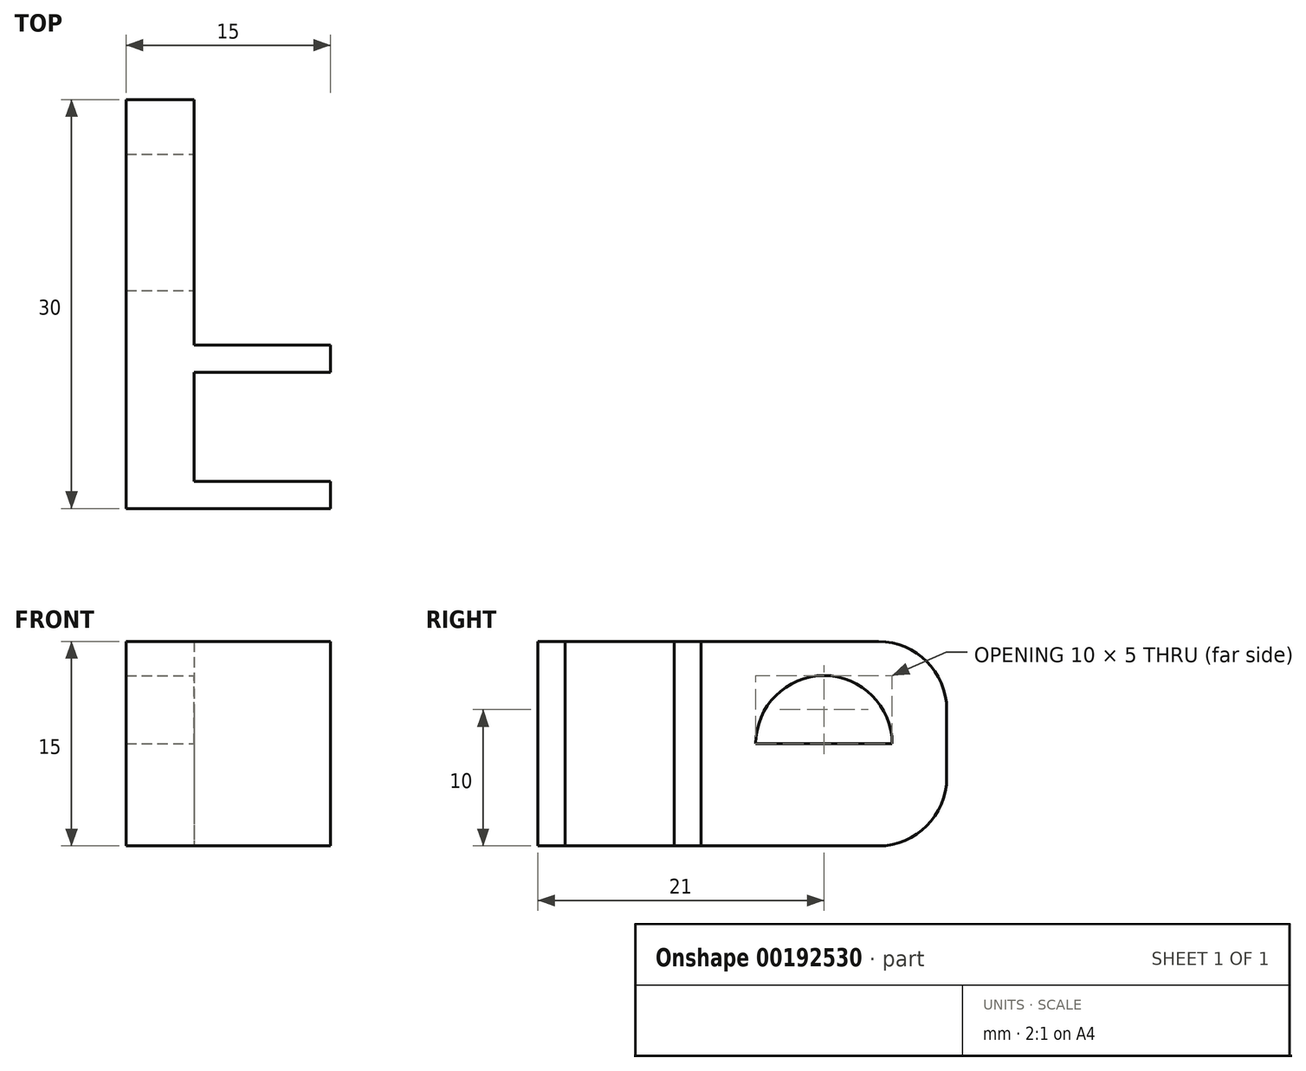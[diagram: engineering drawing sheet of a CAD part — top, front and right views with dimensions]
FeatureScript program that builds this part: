
annotation { "Feature Type Name" : "Feature", "Feature Type Description" : "" }
export const myFeature = defineFeature(function(context is Context, id is Id, definition is map)
    precondition{}
    {
        {
            var Q0;
            Q0=qCreatedBy(makeId("Top.planeOp"),FACE);
            var sketch = newSketch(context, id + "F0", { "sketchPlane" : qUnion([Q0])});
            skLineSegment(sketch, "E0.bottom", {"start": v(0, 0) * mm, "end": v(5, 0) * mm});
            skLineSegment(sketch, "E0.top", {"start": v(0, 30) * mm, "end": v(5, 30) * mm});
            skLineSegment(sketch, "E0.left", {"start": v(0, 0) * mm, "end": v(0, 30) * mm});
            skLineSegment(sketch, "E0.right", {"start": v(5, 0) * mm, "end": v(5, 30) * mm});
            skLineSegment(sketch, "E1.bottom", {"start": v(5, 2) * mm, "end": v(15, 2) * mm});
            skLineSegment(sketch, "E1.top", {"start": v(5, 0) * mm, "end": v(15, 0) * mm});
            skLineSegment(sketch, "E1.left", {"start": v(5, 2) * mm, "end": v(5, 0) * mm});
            skLineSegment(sketch, "E1.right", {"start": v(15, 2) * mm, "end": v(15, 0) * mm});
            skLineSegment(sketch, "E2.bottom", {"start": v(5, 12) * mm, "end": v(15, 12) * mm});
            skLineSegment(sketch, "E2.top", {"start": v(5, 10) * mm, "end": v(15, 10) * mm});
            skLineSegment(sketch, "E2.left", {"start": v(5, 12) * mm, "end": v(5, 10) * mm});
            skLineSegment(sketch, "E2.right", {"start": v(15, 12) * mm, "end": v(15, 10) * mm});
            skSolve(sketch);
        }
        {
            var Q0;
            Q0=makeQuery(id+"F0.imprint","IMPRINT",FACE,{"disambiguationData":[TD([[makeQuery(id+"F0.imprint","IMPRINT",EDGE,{"derivedFrom":sQuery(id+"F0.wireOp",EDGE,"E1.bottom")}),-1.0]])]});
            var Q1;
            Q1=makeQuery(id+"F0.imprint","IMPRINT",FACE,{"disambiguationData":[TD([[makeQuery(id+"F0.imprint","IMPRINT",EDGE,{"derivedFrom":sQuery(id+"F0.wireOp",EDGE,"E2.bottom")}),-1.0]])]});
            var Q2;
            Q2=makeQuery(id+"F0.imprint","IMPRINT",FACE,{"disambiguationData":[TD([[makeQuery(id+"F0.imprint","IMPRINT",EDGE,{"derivedFrom":sQuery(id+"F0.wireOp",EDGE,"E0.bottom")}),1.0]])]});
            extrude(context, id + "F1", {"entities" : qUnion([Q0, Q1, Q2]), "depth" : 15 * mm});
        }
        {
            var Q0;
            {var subQ0=sQuery(id+"F0.wireOp",EDGE,"E0.right");Q0=makeQuery(id+"F1.opExtrude","SWEPT_FACE",FACE,{"disambiguationData":[OSD([subQ0]),TDD([makeQuery(id+"F0.imprint","IMPRINT",EDGE,{"disambiguationData":[TD([[makeQuery(id+"F0.imprint","INTERSECT",VERTEX,{"derivedFrom":[sQuery(id+"F0.wireOp",EDGE,"E0.top"),subQ0]}),1.0]])],"derivedFrom":subQ0})])]});}
            var sketch = newSketch(context, id + "F2", { "sketchPlane" : qUnion([Q0])});
            skCircle(sketch, "E3", {"center": v(21, 7.5) * mm, "radius": 5 * mm});
            skLineSegment(sketch, "E4", {"start": v(21, 15) * mm, "end": v(21, 0) * mm});
            skLineSegment(sketch, "E5", {"start": v(12, 7.5) * mm, "end": v(30, 7.5) * mm});
            skSolve(sketch);
        }
        {
            var Q0;
            {var subQ0=sQuery(id+"F2.wireOp",EDGE,"E4");var subQ1=sQuery(id+"F2.wireOp",EDGE,"E3");var subQ2=makeQuery(id+"F2.imprint","INTERSECT",VERTEX,{"disambiguationData":[OD(0.0)],"derivedFrom":[subQ1,subQ0]});Q0=makeQuery(id+"F2.imprint","IMPRINT",FACE,{"disambiguationData":[TD([[makeQuery(id+"F2.imprint","IMPRINT",EDGE,{"disambiguationData":[TD([[subQ2,1.0]])],"derivedFrom":subQ1}),1.0]])]});}
            var Q1;
            {var subQ0=sQuery(id+"F2.wireOp",EDGE,"E5");var subQ1=sQuery(id+"F2.wireOp",EDGE,"E3");var subQ2=makeQuery(id+"F2.imprint","INTERSECT",VERTEX,{"disambiguationData":[OD(1.0)],"derivedFrom":[subQ1,subQ0]});Q1=makeQuery(id+"F2.imprint","IMPRINT",FACE,{"disambiguationData":[TD([[makeQuery(id+"F2.imprint","IMPRINT",EDGE,{"disambiguationData":[TD([[subQ2,-1.0]])],"derivedFrom":subQ1}),1.0]])]});}
            var Q2;
            {var subQ0=sQuery(id+"F2.wireOp",EDGE,"E5");var subQ1=sQuery(id+"F2.wireOp",EDGE,"E3");var subQ2=makeQuery(id+"F2.imprint","INTERSECT",VERTEX,{"disambiguationData":[OD(0.0)],"derivedFrom":[subQ1,subQ0]});Q2=makeQuery(id+"F2.imprint","IMPRINT",FACE,{"disambiguationData":[TD([[makeQuery(id+"F2.imprint","IMPRINT",EDGE,{"disambiguationData":[TD([[subQ2,1.0]])],"derivedFrom":subQ1}),1.0]])]});}
            var Q3;
            {var subQ0=sQuery(id+"F2.wireOp",EDGE,"E4");var subQ1=sQuery(id+"F2.wireOp",EDGE,"E3");var subQ2=makeQuery(id+"F2.imprint","INTERSECT",VERTEX,{"disambiguationData":[OD(0.0)],"derivedFrom":[subQ1,subQ0]});Q3=makeQuery(id+"F2.imprint","IMPRINT",FACE,{"disambiguationData":[TD([[makeQuery(id+"F2.imprint","IMPRINT",EDGE,{"disambiguationData":[TD([[subQ2,-1.0]])],"derivedFrom":subQ1}),1.0]])]});}
            var Q4;
            Q4=makeQuery(id+"F1.opExtrude","SWEPT_FACE",FACE,{"disambiguationData":[OSD([sQuery(id+"F0.wireOp",EDGE,"E0.left")])]});
            extrude(context, id + "F3", {"entities" : qUnion([Q0, Q1, Q2, Q3]), "operationType" : NewBodyOperationType.REMOVE, "endBound" : BoundingType.UP_TO_SURFACE, "oppositeDirection" : true, "endBoundEntityFace" : qUnion([Q4]), "depth" : 25 * mm});
        }
        {
            var Q0;
            Q0=makeQuery(id+"F1.opExtrude","CAP_EDGE",EDGE,{"disambiguationData":[OSD([sQuery(id+"F0.wireOp",EDGE,"E0.top")])],"isStart":false});
            var Q1;
            Q1=makeQuery(id+"F1.opExtrude","CAP_EDGE",EDGE,{"disambiguationData":[OSD([sQuery(id+"F0.wireOp",EDGE,"E0.top")])],"isStart":true});
            fillet(context, id + "F4", {"entities" : qUnion([Q0, Q1]), "radius" : 5 * mm, "tangentPropagation" : true, "allowEdgeOverflow" : false});
        }
    });
